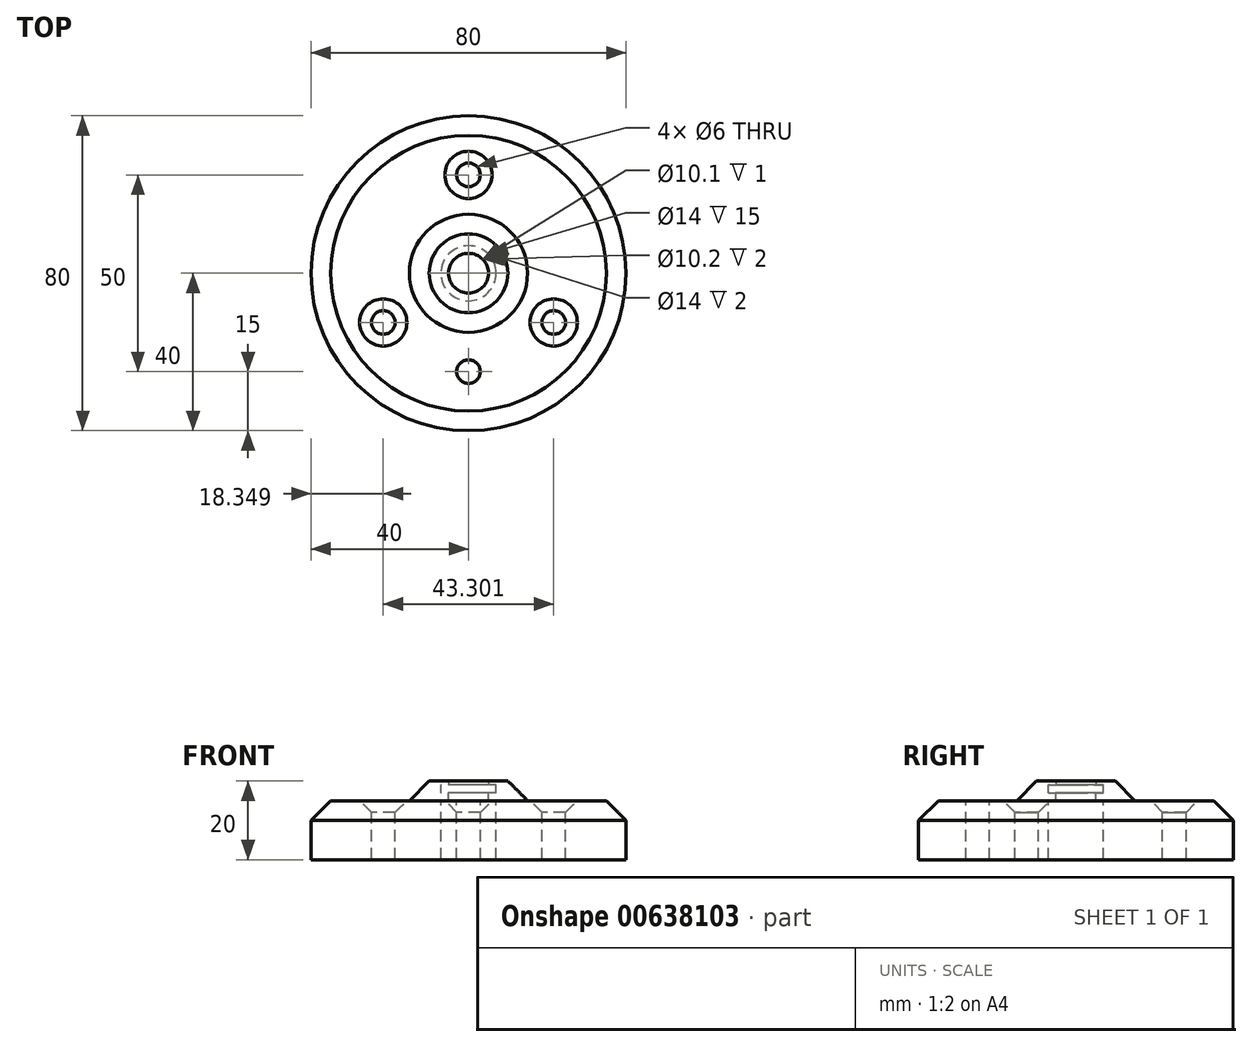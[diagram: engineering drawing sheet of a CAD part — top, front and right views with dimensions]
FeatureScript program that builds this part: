
annotation { "Feature Type Name" : "Feature", "Feature Type Description" : "" }
export const myFeature = defineFeature(function(context is Context, id is Id, definition is map)
    precondition{}
    {
        {
            var Q0;
            Q0=qCreatedBy(makeId("Top.planeOp"),FACE);
            var sketch = newSketch(context, id + "F0", { "sketchPlane" : qUnion([Q0])});
            skCircle(sketch, "E0", {"center": v(0, 0) * mm, "radius": 40 * mm});
            skSolve(sketch);
        }
        {
            var Q0;
            Q0=makeQuery(id+"F0.imprint","IMPRINT",FACE,{"disambiguationData":[TD([[makeQuery(id+"F0.imprint","IMPRINT",EDGE,{"derivedFrom":sQuery(id+"F0.wireOp",EDGE,"E0")}),1.0]])]});
            extrude(context, id + "F1", {"entities" : qUnion([Q0]), "depth" : 15 * mm, "offsetDistance" : 25 * mm});
        }
        {
            var Q0;
            Q0=makeQuery(id+"F1.opExtrude","CAP_EDGE",EDGE,{"disambiguationData":[OSD([sQuery(id+"F0.wireOp",EDGE,"E0")])],"isStart":false});
            chamfer(context, id + "F2", {"entities" : qUnion([Q0]), "width" : 5 * mm, "tangentPropagation" : true});
        }
        {
            var Q0;
            Q0=makeQuery(id+"F1.opExtrude","CAP_FACE",FACE,{"disambiguationData":[OSD([sQuery(id+"F0.wireOp",EDGE,"E0")])],"isStart":false});
            var sketch = newSketch(context, id + "F3", { "sketchPlane" : qUnion([Q0])});
            skCircle(sketch, "E1", {"center": v(0, 0) * mm, "radius": 15 * mm});
            skSolve(sketch);
        }
        {
            var Q0;
            Q0 = qSketchRegion(id + "F3", true);
            extrude(context, id + "F4", {"entities" : qUnion([Q0]), "operationType" : NewBodyOperationType.ADD, "depth" : 5 * mm, "offsetDistance" : 25 * mm});
        }
        {
            var Q0;
            Q0=makeQuery(id+"F4.opExtrude","CAP_EDGE",EDGE,{"disambiguationData":[OSD([sQuery(id+"F3.wireOp",EDGE,"E1")])],"isStart":false});
            chamfer(context, id + "F5", {"entities" : qUnion([Q0]), "width" : 5 * mm, "tangentPropagation" : true});
        }
        {
            var Q0;
            Q0=makeQuery(id+"F1.opExtrude","CAP_FACE",FACE,{"disambiguationData":[OSD([sQuery(id+"F0.wireOp",EDGE,"E0")])],"isStart":false});
            var sketch = newSketch(context, id + "F6", { "sketchPlane" : qUnion([Q0])});
            skLineSegment(sketch, "E2", {"start": v(0, 0) * mm, "end": v(0, 25) * mm});
            skLineSegment(sketch, "E3", {"start": v(0, 0) * mm, "end": v(21.65, -12.5) * mm});
            skLineSegment(sketch, "E4", {"start": v(0, 0) * mm, "end": v(-21.65, -12.5) * mm});
            skLineSegment(sketch, "E5", {"start": v(0, 0) * mm, "end": v(0, -25) * mm});
            skSolve(sketch);
        }
        {
            var Q0;
            Q0=sQuery(id+"F6.wireOp",VERTEX,"E2.end");
            var Q1;
            Q1=sQuery(id+"F6.wireOp",VERTEX,"E4.end");
            var Q2;
            Q2=sQuery(id+"F6.wireOp",VERTEX,"E3.end");
            var Q3;
            Q3=makeQuery(id+"F1.opExtrude","SWEPT_BODY",BODY,{"disambiguationData":[OSD([sQuery(id+"F0.wireOp",EDGE,"E0")])]});
            hole(context, id + "F7", {"style" : HoleStyle.C_SINK, "endStyle" : HoleEndStyle.THROUGH, "holeDiameter" : 6 * mm, "cSinkDiameter" : 12 * mm, "cSinkAngle" : 90 * degree, "majorDiameter" : 5 * mm, "isTappedThrough" : true, "tappedDepth" : 12 * mm, "tapClearance" : 3, "locations" : qUnion([Q0, Q1, Q2]), "scope" : qUnion([Q3])});
        }
        {
            var Q0;
            Q0=sQuery(id+"F0.wireOp",VERTEX,"E0.center");
            var Q1;
            Q1=makeQuery(id+"F1.opExtrude","SWEPT_BODY",BODY,{"disambiguationData":[OSD([sQuery(id+"F0.wireOp",EDGE,"E0")])]});
            hole(context, id + "F8", {"style" : HoleStyle.SIMPLE, "endStyle" : HoleEndStyle.THROUGH, "oppositeDirection" : true, "holeDiameter" : 10.1 * mm, "majorDiameter" : 5 * mm, "isTappedThrough" : true, "tappedDepth" : 12 * mm, "tapClearance" : 3, "locations" : qUnion([Q0]), "scope" : qUnion([Q1])});
        }
        {
            var Q0;
            Q0=qCreatedBy(makeId("Right.planeOp"),FACE);
            var sketch = newSketch(context, id + "F9", { "sketchPlane" : qUnion([Q0])});
            skLineSegment(sketch, "E6", {"start": v(0, 19) * mm, "end": v(7, 19) * mm});
            skLineSegment(sketch, "E7", {"start": v(7, 19) * mm, "end": v(7, 17) * mm});
            skLineSegment(sketch, "E8", {"start": v(7, 17) * mm, "end": v(5.1, 17) * mm});
            skLineSegment(sketch, "E9", {"start": v(5.1, 17) * mm, "end": v(5.1, 15) * mm});
            skLineSegment(sketch, "E10", {"start": v(5.1, 15) * mm, "end": v(7, 15) * mm});
            skLineSegment(sketch, "E11", {"start": v(7, 15) * mm, "end": v(7, 0) * mm});
            skLineSegment(sketch, "E12", {"start": v(7, 0) * mm, "end": v(0, 0) * mm});
            skLineSegment(sketch, "E13", {"start": v(0, 0) * mm, "end": v(0, 19) * mm});
            skSolve(sketch);
        }
        {
            var Q0;
            Q0 = qSketchRegion(id + "F9", true);
            var Q1;
            Q1=sQuery(id+"F9.wireOp",EDGE,"E13");
            revolve(context, id + "F10", {"operationType" : NewBodyOperationType.REMOVE, "entities" : qUnion([Q0]), "axis" : qUnion([Q1]), "revolveType" : RevolveType.FULL, "oppositeDirection" : true});
        }
        {
            var Q0;
            Q0=sQuery(id+"F6.wireOp",VERTEX,"E5.end");
            var Q1;
            Q1=makeQuery(id+"F1.opExtrude","SWEPT_BODY",BODY,{"disambiguationData":[OSD([sQuery(id+"F0.wireOp",EDGE,"E0")])]});
            hole(context, id + "F11", {"style" : HoleStyle.SIMPLE, "endStyle" : HoleEndStyle.THROUGH, "holeDiameter" : 6 * mm, "majorDiameter" : 5 * mm, "isTappedThrough" : true, "tappedDepth" : 12 * mm, "tapClearance" : 3, "locations" : qUnion([Q0]), "scope" : qUnion([Q1])});
        }
    });
